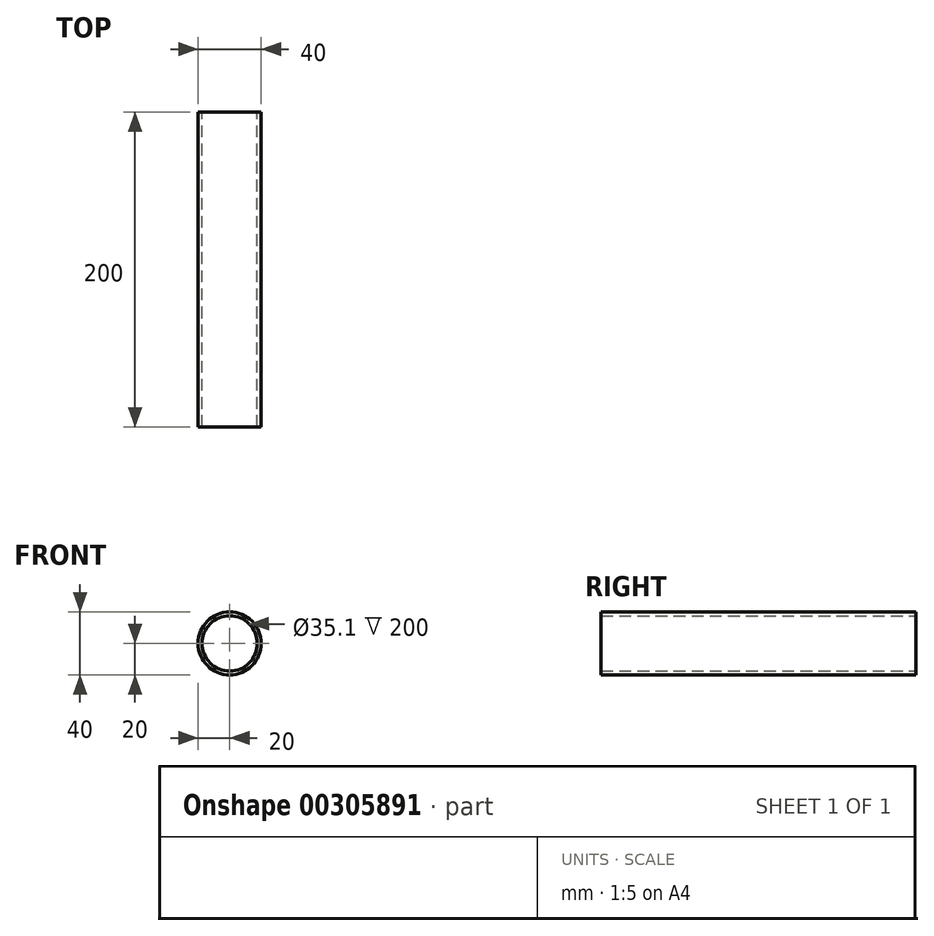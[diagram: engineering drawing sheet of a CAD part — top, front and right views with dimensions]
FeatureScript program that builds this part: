
annotation { "Feature Type Name" : "Feature", "Feature Type Description" : "" }
export const myFeature = defineFeature(function(context is Context, id is Id, definition is map)
    precondition{}
    {
        {
            var Q0;
            Q0=qCreatedBy(makeId("Front.planeOp"),FACE);
            var sketch = newSketch(context, id + "F0", { "sketchPlane" : qUnion([Q0])});
            skCircle(sketch, "E0", {"center": v(0, 0) * mm, "radius": 20 * mm});
            skCircle(sketch, "E1", {"center": v(0, 0) * mm, "radius": 17.55 * mm});
            skSolve(sketch);
        }
        {
            var Q0;
            Q0=makeQuery(id+"F0.imprint","IMPRINT",FACE,{"disambiguationData":[TD([[makeQuery(id+"F0.imprint","IMPRINT",EDGE,{"derivedFrom":sQuery(id+"F0.wireOp",EDGE,"E0")}),1.0]])]});
            extrude(context, id + "F1", {"entities" : qUnion([Q0]), "depth" : 200 * mm});
        }
    });
